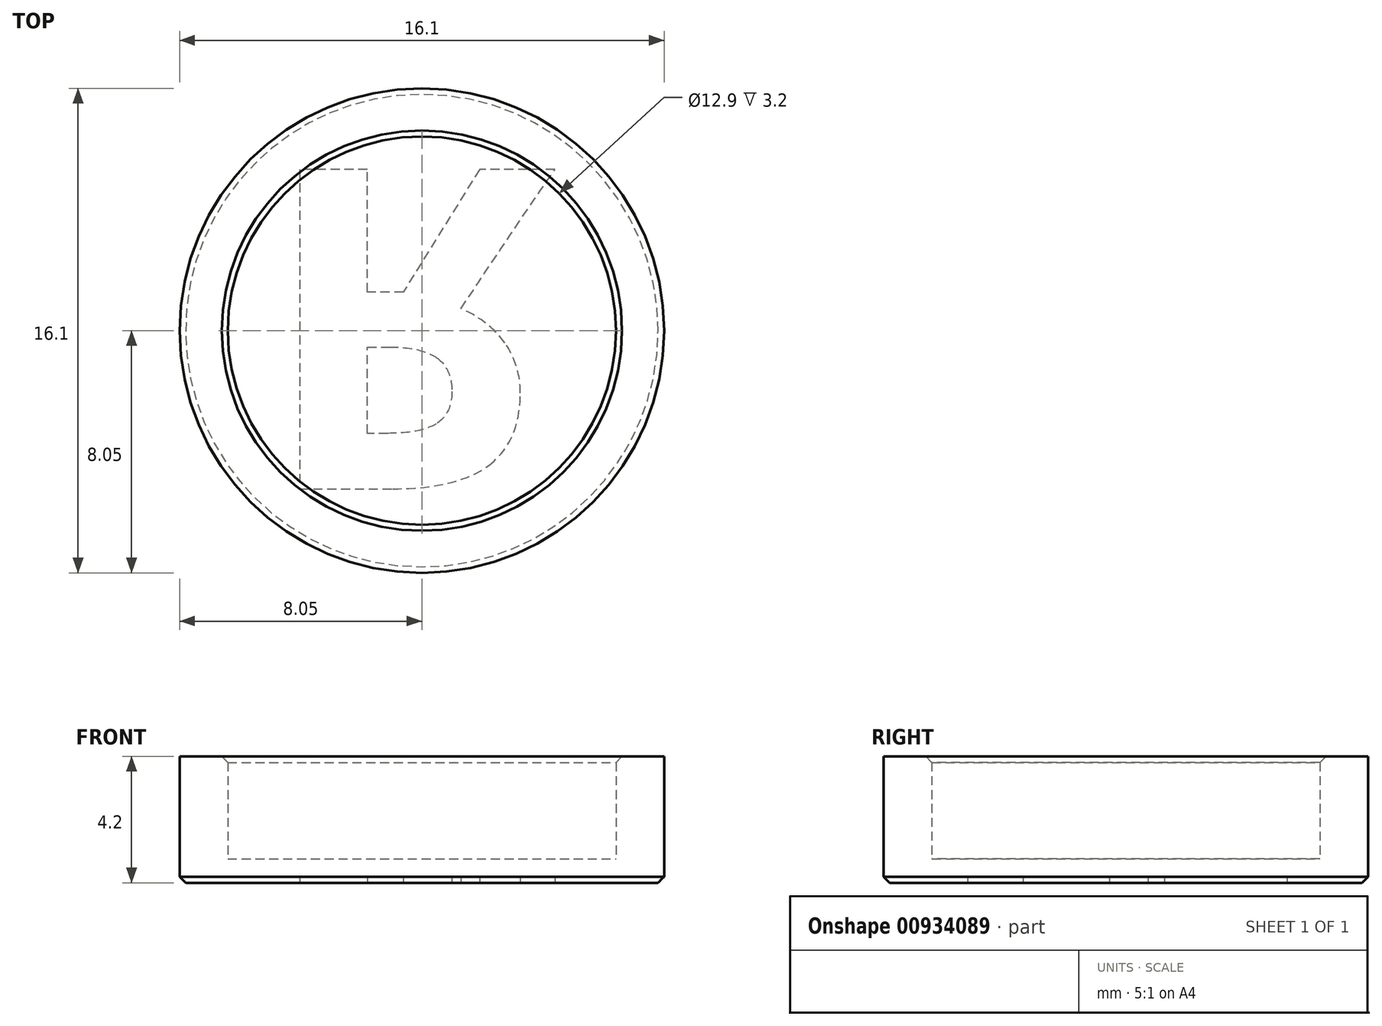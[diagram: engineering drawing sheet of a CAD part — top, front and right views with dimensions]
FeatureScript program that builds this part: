
annotation { "Feature Type Name" : "Feature", "Feature Type Description" : "" }
export const myFeature = defineFeature(function(context is Context, id is Id, definition is map)
    precondition{}
    {
        {
            var Q0;
            Q0=qCreatedBy(makeId("Front.planeOp"),FACE);
            var sketch = newSketch(context, id + "F0", { "sketchPlane" : qUnion([Q0])});
            skLineSegment(sketch, "E0", {"start": v(0, 0) * mm, "end": v(-6.45, 0) * mm});
            skLineSegment(sketch, "E1", {"start": v(-6.45, 0) * mm, "end": v(-6.45, 3.4) * mm});
            skLineSegment(sketch, "E2", {"start": v(-6.45, 3.4) * mm, "end": v(-8.05, 3.4) * mm});
            skLineSegment(sketch, "E3", {"start": v(-8.05, 3.4) * mm, "end": v(-8.05, -0.8) * mm});
            skLineSegment(sketch, "E4", {"start": v(-8.05, -0.8) * mm, "end": v(0, -0.8) * mm});
            skLineSegment(sketch, "E5", {"start": v(0, -0.8) * mm, "end": v(0, 0) * mm});
            skSolve(sketch);
        }
        {
            var Q0;
            Q0 = qSketchRegion(id + "F0", true);
            var Q1;
            Q1=sQuery(id+"F0.wireOp",EDGE,"E5");
            revolve(context, id + "F1", {"surfaceOperationType" : NewSurfaceOperationType.NEW, "entities" : qUnion([Q0]), "axis" : qUnion([Q1]), "revolveType" : RevolveType.FULL});
        }
        {
            var Q0;
            Q0=makeQuery(id+"F1.opRevolve","SWEPT_FACE",FACE,{"disambiguationData":[OSD([sQuery(id+"F0.wireOp",EDGE,"E4")])]});
            var Q1;
            Q1=makeQuery(id+"F1.opRevolve","SWEPT_EDGE",EDGE,{"disambiguationData":[OSD([sQuery(id+"F0.wireOp",EDGE,"E1"),sQuery(id+"F0.wireOp",EDGE,"E2")])]});
            chamfer(context, id + "F2", {"entities" : qUnion([Q0, Q1]), "width" : 0.2 * mm});
        }
        {
            var Q0;
            Q0=makeQuery(id+"F1.opRevolve","SWEPT_FACE",FACE,{"disambiguationData":[OSD([sQuery(id+"F0.wireOp",EDGE,"E4")])]});
            var sketch = newSketch(context, id + "F3", { "sketchPlane" : qUnion([Q0])});
            skText(sketch, "E6", { "text": "R", "fontName": "OpenSans-Bold.ttf"});
            const initialGuessF3  = {"E6": [-0.0054, -0.00536, 1, 0, 0.01071]};
            skSetInitialGuess(sketch, initialGuessF3);
            skSolve(sketch);
        }
        {
            var Q0;
            Q0 = qSketchRegion(id + "F3", true);
            extrude(context, id + "F4", {"entities" : qUnion([Q0]), "operationType" : NewBodyOperationType.REMOVE, "oppositeDirection" : true, "depth" : 0.2 * mm, "offsetDistance" : 25 * mm});
        }
    });
